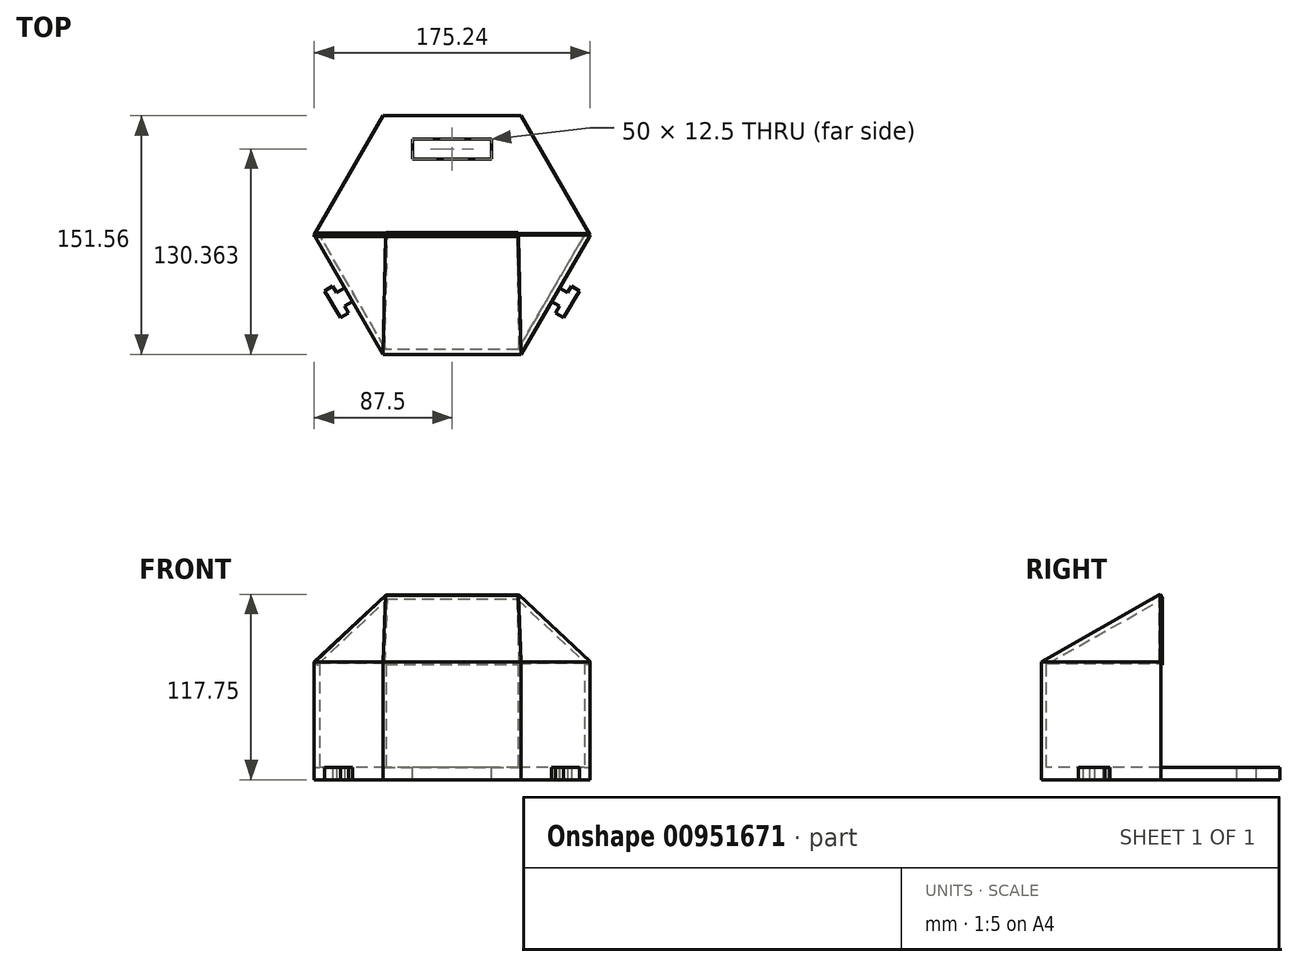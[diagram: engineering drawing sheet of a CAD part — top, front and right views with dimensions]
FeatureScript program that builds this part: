
annotation { "Feature Type Name" : "Feature", "Feature Type Description" : "" }
export const myFeature = defineFeature(function(context is Context, id is Id, definition is map)
    precondition{}
    {
        {
            var Q0;
            Q0=qCreatedBy(makeId("Top.planeOp"),FACE);
            var sketch = newSketch(context, id + "F0", { "sketchPlane" : qUnion([Q0])});
            skCircle(sketch, "E0.cCircle", {"center": v(0, 0) * mm, "radius": 75.78 * mm, "construction": true});
            skLineSegment(sketch, "E0.0", {"start": v(-43.75, 75.78) * mm, "end": v(43.75, 75.78) * mm});
            skLineSegment(sketch, "E0.1", {"start": v(43.75, 75.78) * mm, "end": v(87.5, 0) * mm});
            skLineSegment(sketch, "E0.2", {"start": v(87.5, 0) * mm, "end": v(43.75, -75.78) * mm});
            skLineSegment(sketch, "E0.3", {"start": v(43.75, -75.78) * mm, "end": v(-43.75, -75.78) * mm});
            skLineSegment(sketch, "E0.4", {"start": v(-43.75, -75.78) * mm, "end": v(-87.5, 0) * mm});
            skLineSegment(sketch, "E0.5", {"start": v(-87.5, 0) * mm, "end": v(-43.75, 75.78) * mm});
            skPoint(sketch, "E0.0.midPoint", {"position": v(0, 75.78) * mm});
            skLineSegment(sketch, "E1.0", {"start": v(-84.04, 0) * mm, "end": v(-42.02, 72.78) * mm});
            skLineSegment(sketch, "E1.1", {"start": v(42.02, 72.78) * mm, "end": v(84.04, 0) * mm});
            skLineSegment(sketch, "E1.2", {"start": v(84.04, 0) * mm, "end": v(42.02, -72.78) * mm});
            skLineSegment(sketch, "E1.3", {"start": v(-42.02, 72.78) * mm, "end": v(42.02, 72.78) * mm});
            skLineSegment(sketch, "E1.4", {"start": v(42.02, -72.78) * mm, "end": v(-42.02, -72.78) * mm});
            skLineSegment(sketch, "E1.5", {"start": v(-42.02, -72.78) * mm, "end": v(-84.04, 0) * mm});
            skLineSegment(sketch, "E2", {"start": v(-87.5, 0) * mm, "end": v(-84.04, 0) * mm});
            skLineSegment(sketch, "E3", {"start": v(84.04, 0) * mm, "end": v(87.5, 0) * mm});
            skLineSegment(sketch, "E4", {"start": v(0, 0) * mm, "end": v(0, 72.78) * mm, "construction": true});
            skLineSegment(sketch, "E5", {"start": v(0, 0) * mm, "end": v(42.02, 72.78) * mm, "construction": true});
            skLineSegment(sketch, "E6", {"start": v(0, 0) * mm, "end": v(-42.02, 72.78) * mm, "construction": true});
            skLineSegment(sketch, "E7", {"start": v(0, 36.39) * mm, "end": v(0, 72.78) * mm, "construction": true});
            skLineSegment(sketch, "E8.bottom", {"start": v(25, 48.33) * mm, "end": v(-25, 48.33) * mm});
            skLineSegment(sketch, "E8.top", {"start": v(25, 60.83) * mm, "end": v(-25, 60.83) * mm});
            skLineSegment(sketch, "E8.left", {"start": v(25, 48.33) * mm, "end": v(25, 60.83) * mm});
            skLineSegment(sketch, "E8.right", {"start": v(-25, 48.33) * mm, "end": v(-25, 60.83) * mm});
            skPoint(sketch, "E8.middle", {"position": v(0, 54.58) * mm});
            skLineSegment(sketch, "E9", {"start": v(-65.63, 37.89) * mm, "end": v(-68.13, 33.56) * mm});
            skLineSegment(sketch, "E10.MirrorCS", {"start": v(87.5, 0) * mm, "end": v(43.75, 75.78) * mm});
            skLineSegment(sketch, "E11.MirrorCS", {"start": v(-78.45, -39.68) * mm, "end": v(-68.12, -33.56) * mm});
            skLineSegment(sketch, "E12.MirrorCS", {"start": v(-73.33, -36.65) * mm, "end": v(-75.88, -32.34) * mm});
            skLineSegment(sketch, "E13.MirrorCS", {"start": v(-75.88, -32.34) * mm, "end": v(-80.95, -35.46) * mm});
            skLineSegment(sketch, "E14.MirrorCS", {"start": v(-78.45, -39.68) * mm, "end": v(-81, -35.38) * mm});
            skLineSegment(sketch, "E15.MirrorCS", {"start": v(-78.45, -39.68) * mm, "end": v(-73.4, -48.2) * mm});
            skLineSegment(sketch, "E16.MirrorCS", {"start": v(-73.4, -48.2) * mm, "end": v(-70.88, -52.4) * mm});
            skLineSegment(sketch, "E17.MirrorCS", {"start": v(-65.74, -49.4) * mm, "end": v(-70.88, -52.4) * mm});
            skLineSegment(sketch, "E18.MirrorCS", {"start": v(-68.26, -45.15) * mm, "end": v(-65.74, -49.4) * mm});
            skLineSegment(sketch, "E19.MirrorCS", {"start": v(-73.4, -48.2) * mm, "end": v(-63.12, -42.1) * mm});
            skLineSegment(sketch, "E20", {"start": v(-73.4, -48.2) * mm, "end": v(-68.26, -45.15) * mm});
            skPoint(sketch, "E20.endSnap0", {"position": v(-68.26, -45.15) * mm});
            skLineSegment(sketch, "E21.MirrorCS", {"start": v(68.26, -45.15) * mm, "end": v(65.74, -49.4) * mm});
            skLineSegment(sketch, "E22.MirrorCS", {"start": v(65.74, -49.4) * mm, "end": v(70.88, -52.4) * mm});
            skLineSegment(sketch, "E23.MirrorCS", {"start": v(73.4, -48.2) * mm, "end": v(70.88, -52.4) * mm});
            skLineSegment(sketch, "E24.MirrorCS", {"start": v(73.4, -48.2) * mm, "end": v(63.12, -42.1) * mm});
            skLineSegment(sketch, "E25.MirrorCS", {"start": v(78.45, -39.68) * mm, "end": v(73.4, -48.2) * mm});
            skLineSegment(sketch, "E26.MirrorCS", {"start": v(78.45, -39.68) * mm, "end": v(68.12, -33.56) * mm});
            skLineSegment(sketch, "E27.MirrorCS", {"start": v(73.33, -36.65) * mm, "end": v(75.88, -32.34) * mm});
            skLineSegment(sketch, "E28.MirrorCS", {"start": v(75.88, -32.34) * mm, "end": v(80.95, -35.46) * mm});
            skLineSegment(sketch, "E29.MirrorCS", {"start": v(78.45, -39.68) * mm, "end": v(81, -35.38) * mm});
            skSolve(sketch);
        }
        {
            var Q0;
            Q0=makeQuery(id+"F0.imprint","IMPRINT",FACE,{"disambiguationData":[TD([[makeQuery(id+"F0.imprint","IMPRINT",EDGE,{"derivedFrom":sQuery(id+"F0.wireOp",EDGE,"E1.0")}),-1.0]])]});
            extrude(context, id + "F1", {"entities" : qUnion([Q0]), "depth" : 8 * mm, "offsetDistance" : 25 * mm});
        }
        {
            var Q0;
            Q0=makeQuery(id+"F0.imprint","IMPRINT",FACE,{"disambiguationData":[TD([[makeQuery(id+"F0.imprint","IMPRINT",EDGE,{"derivedFrom":sQuery(id+"F0.wireOp",EDGE,"E0.2")}),-1.0]])]});
            extrude(context, id + "F2", {"entities" : qUnion([Q0]), "operationType" : NewBodyOperationType.ADD, "depth" : 75 * mm, "offsetDistance" : 25 * mm});
        }
        {
            var Q0;
            Q0=qCreatedBy(makeId("Front.planeOp"),FACE);
            var sketch = newSketch(context, id + "F3", { "sketchPlane" : qUnion([Q0])});
            skLineSegment(sketch, "E30", {"start": v(0, 0) * mm, "end": v(0, 144.27) * mm, "construction": true});
            skLineSegment(sketch, "E31", {"start": v(0, 144.27) * mm, "end": v(-94, 144.27) * mm, "construction": true});
            skLineSegment(sketch, "E32", {"start": v(0, 144.27) * mm, "end": v(81.74, 144.27) * mm});
            skLineSegment(sketch, "E33", {"start": v(0, 0) * mm, "end": v(0, 75) * mm, "construction": true});
            skLineSegment(sketch, "E34", {"start": v(0, 75) * mm, "end": v(0, 114.5) * mm, "construction": true});
            skLineSegment(sketch, "E35", {"start": v(0, 75) * mm, "end": v(-87.5, 75) * mm, "construction": true});
            skLineSegment(sketch, "E36", {"start": v(0, 114.5) * mm, "end": v(42.02, 114.5) * mm, "construction": true});
            skLineSegment(sketch, "E37", {"start": v(0, 114.5) * mm, "end": v(-42.02, 114.5) * mm});
            skLineSegment(sketch, "E38", {"start": v(0, 75) * mm, "end": v(-84.04, 75) * mm, "construction": true});
            skLineSegment(sketch, "E39", {"start": v(-42.02, 114.5) * mm, "end": v(-84.04, 75) * mm});
            skLineSegment(sketch, "E40", {"start": v(-42.02, 114.5) * mm, "end": v(-42.02, 117.5) * mm, "construction": true});
            skLineSegment(sketch, "E41", {"start": v(-42.02, 117.5) * mm, "end": v(-87.5, 75) * mm});
            skLineSegment(sketch, "E42", {"start": v(-42.02, 117.5) * mm, "end": v(0, 117.5) * mm});
            skLineSegment(sketch, "E43.MirrorCS", {"start": v(42.02, 117.5) * mm, "end": v(87.5, 75) * mm});
            skLineSegment(sketch, "E44.MirrorCS", {"start": v(42.02, 114.5) * mm, "end": v(84.04, 75) * mm});
            skLineSegment(sketch, "E45.MirrorCS", {"start": v(42.02, 117.5) * mm, "end": v(0, 117.5) * mm});
            skLineSegment(sketch, "E46.MirrorCS", {"start": v(0, 114.5) * mm, "end": v(42.02, 114.5) * mm});
            skLineSegment(sketch, "E47", {"start": v(87.5, 75) * mm, "end": v(84.04, 75) * mm});
            skLineSegment(sketch, "E48", {"start": v(-84.04, 75) * mm, "end": v(-87.5, 75) * mm});
            skSolve(sketch);
        }
        {
            var Q0;
            Q0=makeQuery(id+"F0.imprint","IMPRINT",FACE,{"disambiguationData":[TD([[makeQuery(id+"F0.imprint","IMPRINT",EDGE,{"derivedFrom":sQuery(id+"F0.wireOp",EDGE,"E0.0")}),-1.0]])]});
            extrude(context, id + "F4", {"entities" : qUnion([Q0]), "operationType" : NewBodyOperationType.ADD, "oppositeDirection" : true, "depth" : -8 * mm, "offsetDistance" : 25 * mm});
        }
        {
            var Q0;
            Q0=makeQuery(id+"F2.opExtrude","CAP_EDGE",EDGE,{"disambiguationData":[OSD([sQuery(id+"F0.wireOp",EDGE,"E0.3")])],"isStart":false});
            var Q1;
            Q1=sQuery(id+"F3.wireOp",VERTEX,"E42.end");
            cPlane(context, id + "F5", {"entities" : qUnion([Q0, Q1]), "cplaneType" : CPlaneType.LINE_ANGLE, "offset" : 25 * mm, "angle" : 0 * degree, "width" : 150 * mm, "height" : 150 * mm});
        }
        {
            var Q0;
            Q0=qCreatedBy(id+"F5.planeOp",FACE);
            var sketch = newSketch(context, id + "F6", { "sketchPlane" : qUnion([Q0])});
            skLineSegment(sketch, "E49", {"start": v(0, 29.4) * mm, "end": v(43.75, 29.4) * mm});
            skLineSegment(sketch, "E50", {"start": v(0, 29.4) * mm, "end": v(-43.75, 29.4) * mm});
            skLineSegment(sketch, "E51", {"start": v(-43.75, 29.4) * mm, "end": v(-42.02, -57.48) * mm});
            skLineSegment(sketch, "E52", {"start": v(43.75, 29.4) * mm, "end": v(42.02, -57.48) * mm});
            skLineSegment(sketch, "E53", {"start": v(-42.02, -57.48) * mm, "end": v(42.02, -57.48) * mm});
            skSolve(sketch);
        }
        {
            var Q0;
            Q0=makeQuery(id+"F6.imprint","IMPRINT",FACE,{"disambiguationData":[TD([[makeQuery(id+"F6.imprint","IMPRINT",EDGE,{"derivedFrom":sQuery(id+"F6.wireOp",EDGE,"E49")}),-1.0]])]});
            extrude(context, id + "F7", {"entities" : qUnion([Q0]), "operationType" : NewBodyOperationType.ADD, "depth" : 3 * mm, "offsetDistance" : 25 * mm});
        }
        {
            var Q0;
            Q0=makeQuery(id+"F3.imprint","IMPRINT",FACE,{"disambiguationData":[TD([[makeQuery(id+"F3.imprint","IMPRINT",EDGE,{"derivedFrom":sQuery(id+"F3.wireOp",EDGE,"E37")}),-1.0]])]});
            extrude(context, id + "F8", {"entities" : qUnion([Q0]), "operationType" : NewBodyOperationType.ADD, "depth" : 1 * mm, "offsetDistance" : 25 * mm});
        }
        {
            var Q0;
            Q0=makeQuery(id+"F8.opExtrude","CAP_EDGE",EDGE,{"disambiguationData":[OSD([sQuery(id+"F3.wireOp",EDGE,"E41")])],"isStart":true});
            var Q1;
            Q1=makeQuery(id+"F7.boolean.opBoolean","MERGE",VERTEX,{"derivedFrom":[makeQuery(id+"F2.opExtrude","CAP_VERTEX",VERTEX,{"disambiguationData":[OSD([sQuery(id+"F0.wireOp",EDGE,"E0.3"),sQuery(id+"F0.wireOp",EDGE,"E0.4")])],"isStart":false}),makeQuery(id+"F7.opExtrude","CAP_VERTEX",VERTEX,{"disambiguationData":[OSD([sQuery(id+"F6.wireOp",EDGE,"E50"),sQuery(id+"F6.wireOp",EDGE,"E51")])],"isStart":true})]});
            cPlane(context, id + "F9", {"entities" : qUnion([Q0, Q1]), "cplaneType" : CPlaneType.LINE_ANGLE, "offset" : 25 * mm, "angle" : 0 * degree, "width" : 150 * mm, "height" : 150 * mm});
        }
        {
            var Q0;
            Q0=qCreatedBy(id+"F9.planeOp",FACE);
            var sketch = newSketch(context, id + "F10", { "sketchPlane" : qUnion([Q0])});
            skLineSegment(sketch, "E54", {"start": v(-25.66, 35.61) * mm, "end": v(30.99, -31.08) * mm});
            skLineSegment(sketch, "E55", {"start": v(-25.66, 35.61) * mm, "end": v(33.23, 55.79) * mm});
            skLineSegment(sketch, "E56", {"start": v(33.23, 55.79) * mm, "end": v(30.99, -31.08) * mm});
            skSolve(sketch);
        }
        {
            var Q0;
            Q0=qSketchRegion(id+"F10",true);
            extrude(context, id + "F11", {"entities" : qUnion([Q0]), "operationType" : NewBodyOperationType.ADD, "depth" : -3 * mm, "offsetDistance" : 25 * mm});
        }
        {
            var Q0;
            Q0=makeQuery(id+"F8.opExtrude","CAP_EDGE",EDGE,{"disambiguationData":[OSD([sQuery(id+"F3.wireOp",EDGE,"E43.MirrorCS")])],"isStart":false});
            var Q1;
            Q1=makeQuery(id+"F7.boolean.opBoolean","MERGE",VERTEX,{"derivedFrom":[makeQuery(id+"F2.opExtrude","CAP_VERTEX",VERTEX,{"disambiguationData":[OSD([sQuery(id+"F0.wireOp",EDGE,"E0.2"),sQuery(id+"F0.wireOp",EDGE,"E0.3")])],"isStart":false}),makeQuery(id+"F7.opExtrude","CAP_VERTEX",VERTEX,{"disambiguationData":[OSD([sQuery(id+"F6.wireOp",EDGE,"E49"),sQuery(id+"F6.wireOp",EDGE,"E52")])],"isStart":true})]});
            cPlane(context, id + "F12", {"entities" : qUnion([Q0, Q1]), "cplaneType" : CPlaneType.LINE_ANGLE, "offset" : 25 * mm, "angle" : 0 * degree, "width" : 150 * mm, "height" : 150 * mm});
        }
        {
            var Q0;
            Q0=qCreatedBy(id+"F12.planeOp",FACE);
            var sketch = newSketch(context, id + "F13", { "sketchPlane" : qUnion([Q0])});
            skLineSegment(sketch, "E57", {"start": v(-32.88, -56.36) * mm, "end": v(25.94, -35.98) * mm});
            skLineSegment(sketch, "E58", {"start": v(25.94, -35.98) * mm, "end": v(-30.94, 30.51) * mm});
            skLineSegment(sketch, "E59", {"start": v(-30.94, 30.51) * mm, "end": v(-32.88, -56.36) * mm});
            skSolve(sketch);
        }
        {
            var Q0;
            Q0=qSketchRegion(id+"F13",true);
            extrude(context, id + "F14", {"entities" : qUnion([Q0]), "operationType" : NewBodyOperationType.ADD, "depth" : 3 * mm, "offsetDistance" : 25 * mm});
        }
        {
            var Q0;
            Q0=makeQuery(id+"F0.imprint","IMPRINT",FACE,{"disambiguationData":[TD([[makeQuery(id+"F0.imprint","IMPRINT",EDGE,{"derivedFrom":sQuery(id+"F0.wireOp",EDGE,"E8.bottom")}),-1.0]])]});
            extrude(context, id + "F15", {"entities" : qUnion([Q0]), "operationType" : NewBodyOperationType.ADD, "depth" : 8 * mm, "offsetDistance" : 25 * mm});
        }
        {
            var Q0;
            {var subQ5=sQuery(id+"F0.wireOp",EDGE,"E13.MirrorCS");Q0=makeQuery(id+"F0.imprint","IMPRINT",FACE,{"disambiguationData":[TD([[makeQuery(id+"F0.imprint","IMPRINT",EDGE,{"derivedFrom":subQ5}),1.0]])]});}
            var Q1;
            {var subQ4=sQuery(id+"F0.wireOp",EDGE,"E15.MirrorCS");Q1=makeQuery(id+"F0.imprint","IMPRINT",FACE,{"disambiguationData":[TD([[makeQuery(id+"F0.imprint","IMPRINT",EDGE,{"derivedFrom":subQ4}),1.0]])]});}
            var Q2;
            {var subQ0=sQuery(id+"F0.wireOp",EDGE,"E16.MirrorCS");Q2=makeQuery(id+"F0.imprint","IMPRINT",FACE,{"disambiguationData":[TD([[makeQuery(id+"F0.imprint","IMPRINT",EDGE,{"derivedFrom":subQ0}),1.0]])]});}
            var Q3;
            {var subQ5=sQuery(id+"F0.wireOp",EDGE,"E28.MirrorCS");Q3=makeQuery(id+"F0.imprint","IMPRINT",FACE,{"disambiguationData":[TD([[makeQuery(id+"F0.imprint","IMPRINT",EDGE,{"derivedFrom":subQ5}),-1.0]])]});}
            var Q4;
            {var subQ0=sQuery(id+"F0.wireOp",EDGE,"E25.MirrorCS");Q4=makeQuery(id+"F0.imprint","IMPRINT",FACE,{"disambiguationData":[TD([[makeQuery(id+"F0.imprint","IMPRINT",EDGE,{"derivedFrom":subQ0}),-1.0]])]});}
            var Q5;
            {var subQ0=sQuery(id+"F0.wireOp",EDGE,"E21.MirrorCS");Q5=makeQuery(id+"F0.imprint","IMPRINT",FACE,{"disambiguationData":[TD([[makeQuery(id+"F0.imprint","IMPRINT",EDGE,{"derivedFrom":subQ0}),1.0]])]});}
            extrude(context, id + "F16", {"entities" : qUnion([Q0, Q1, Q2, Q3, Q4, Q5]), "operationType" : NewBodyOperationType.ADD, "depth" : 8 * mm, "offsetDistance" : 25 * mm});
        }
        {
            var Q0;
            Q0=makeQuery(id+"F0.imprint","IMPRINT",FACE,{"disambiguationData":[TD([[makeQuery(id+"F0.imprint","IMPRINT",EDGE,{"derivedFrom":sQuery(id+"F0.wireOp",EDGE,"E8.bottom")}),-1.0]])]});
            extrude(context, id + "F17", {"entities" : qUnion([Q0]), "operationType" : NewBodyOperationType.REMOVE, "endBound" : BoundingType.SYMMETRIC, "oppositeDirection" : true, "depth" : 25 * mm, "offsetDistance" : 25 * mm});
        }
    });
